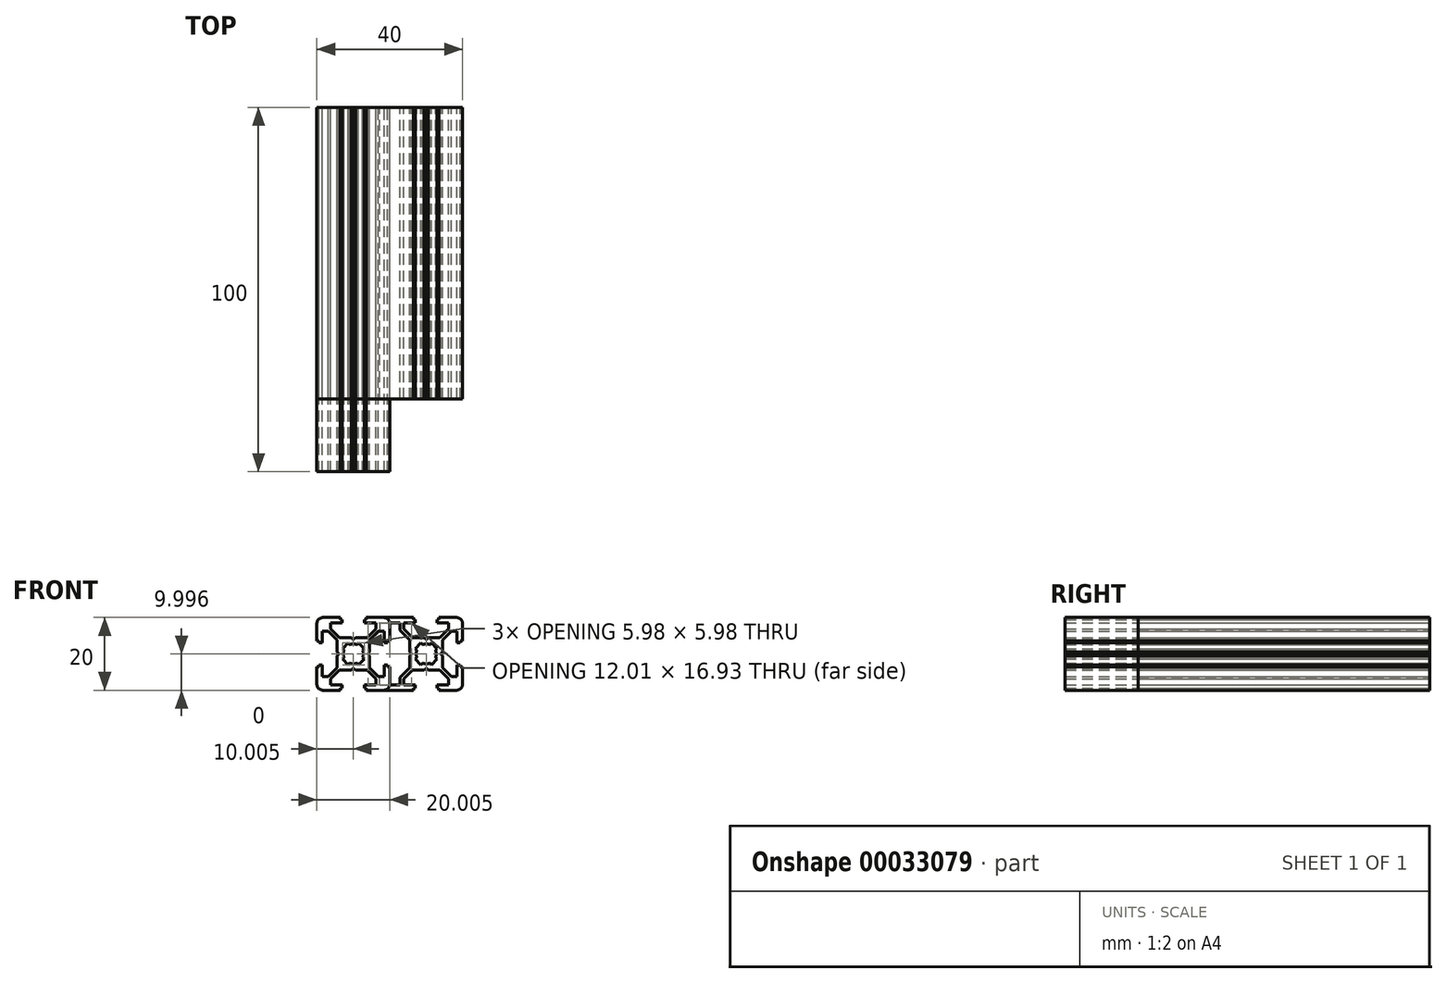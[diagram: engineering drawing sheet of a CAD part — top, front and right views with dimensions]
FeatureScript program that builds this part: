
annotation { "Feature Type Name" : "Feature", "Feature Type Description" : "" }
export const myFeature = defineFeature(function(context is Context, id is Id, definition is map)
    precondition{}
    {
        {
            var Q0;
            Q0=qCreatedBy(makeId("Front.planeOp"),FACE);
            var sketch = newSketch(context, id + "F0", { "sketchPlane" : qUnion([Q0])});
            skLineSegment(sketch, "E0.rect.bottom", {"start": v(-8.26, 10.09) * mm, "end": v(-3.52, 10.09) * mm});
            skLineSegment(sketch, "E0.rect.top", {"start": v(-8.26, -9.91) * mm, "end": v(-3.52, -9.91) * mm});
            skLineSegment(sketch, "E0.rect.left", {"start": v(-10, 8.34) * mm, "end": v(-10, 3.6) * mm});
            skLineSegment(sketch, "E0.rect.right", {"start": v(10, 8.34) * mm, "end": v(10, 3.6) * mm});
            skPoint(sketch, "E0.rect.middle", {"position": v(0, 0.09) * mm});
            skPoint(sketch, "E1.visualSharp", {"position": v(-10, 10.09) * mm});
            skArc(sketch, "E1.filletArc", {"start": v(-8.26, 10.09) * mm, "mid": v(-9.5, 9.57) * mm, "end": v(-10, 8.34) * mm});
            skPoint(sketch, "E2.visualSharp", {"position": v(10, 10.09) * mm});
            skArc(sketch, "E2.filletArc", {"start": v(10, 8.34) * mm, "mid": v(9.48, 9.57) * mm, "end": v(8.24, 10.09) * mm});
            skPoint(sketch, "E3.visualSharp", {"position": v(10, -9.91) * mm});
            skArc(sketch, "E3.filletArc", {"start": v(8.24, -9.91) * mm, "mid": v(9.48, -9.4) * mm, "end": v(10, -8.16) * mm});
            skPoint(sketch, "E4.visualSharp", {"position": v(-10, -9.91) * mm});
            skArc(sketch, "E4.filletArc", {"start": v(-10, -8.16) * mm, "mid": v(-9.5, -9.4) * mm, "end": v(-8.26, -9.91) * mm});
            skPoint(sketch, "E5.rect.middle", {"position": v(-10, 0.09) * mm});
            skPoint(sketch, "E6.rect.middle", {"position": v(0, -9.91) * mm});
            skPoint(sketch, "E7.4.MirrorP", {"position": v(0, 10.09) * mm});
            skPoint(sketch, "E8.4.MirrorP", {"position": v(10, 0.09) * mm});
            skLineSegment(sketch, "E9", {"start": v(-3, 9.47) * mm, "end": v(-3, 8.55) * mm});
            skLineSegment(sketch, "E10", {"start": v(-3, 8.55) * mm, "end": v(-6.2, 8.55) * mm});
            skLineSegment(sketch, "E11", {"start": v(-6.2, 8.55) * mm, "end": v(-6.2, 6.99) * mm});
            skLineSegment(sketch, "E12", {"start": v(-0.58, 4.59) * mm, "end": v(-3.8, 4.59) * mm});
            skLineSegment(sketch, "E13", {"start": v(-3.8, 4.59) * mm, "end": v(-6.2, 6.99) * mm});
            skLineSegment(sketch, "E14", {"start": v(-3.52, 10.09) * mm, "end": v(-3.52, 9.47) * mm});
            skLineSegment(sketch, "E15", {"start": v(-3.52, 9.47) * mm, "end": v(-3, 9.47) * mm});
            skLineSegment(sketch, "E16", {"start": v(0, 28.9) * mm, "end": v(0, 4.59) * mm});
            skLineSegment(sketch, "E17.0.MirrorCS", {"start": v(3.51, 10.09) * mm, "end": v(3.51, 9.47) * mm});
            skLineSegment(sketch, "E18.0.MirrorCS", {"start": v(3.51, 9.47) * mm, "end": v(3, 9.47) * mm});
            skLineSegment(sketch, "E19.0.MirrorCS", {"start": v(3, 8.55) * mm, "end": v(6.2, 8.55) * mm});
            skLineSegment(sketch, "E20.0.MirrorCS", {"start": v(6.2, 8.55) * mm, "end": v(6.2, 6.99) * mm});
            skLineSegment(sketch, "E21.0.MirrorCS", {"start": v(3.8, 4.59) * mm, "end": v(6.2, 6.99) * mm});
            skLineSegment(sketch, "E22.0.MirrorCS", {"start": v(3.51, -9.91) * mm, "end": v(3.51, -9.3) * mm});
            skLineSegment(sketch, "E23.0.MirrorCS", {"start": v(3.51, -9.3) * mm, "end": v(3, -9.3) * mm});
            skLineSegment(sketch, "E24.0.MirrorCS", {"start": v(3, -8.38) * mm, "end": v(6.2, -8.38) * mm});
            skLineSegment(sketch, "E25.0.MirrorCS", {"start": v(6.2, -8.38) * mm, "end": v(6.2, -6.81) * mm});
            skLineSegment(sketch, "E26.0.MirrorCS", {"start": v(3.8, -4.41) * mm, "end": v(6.2, -6.81) * mm});
            skLineSegment(sketch, "E27.0.MirrorCS", {"start": v(-0.58, -4.41) * mm, "end": v(-3.8, -4.41) * mm});
            skLineSegment(sketch, "E28.0.MirrorCS", {"start": v(-3.8, -4.41) * mm, "end": v(-6.2, -6.81) * mm});
            skLineSegment(sketch, "E29.0.MirrorCS", {"start": v(-6.2, -8.38) * mm, "end": v(-6.2, -6.81) * mm});
            skLineSegment(sketch, "E30.0.MirrorCS", {"start": v(-3, -8.38) * mm, "end": v(-6.2, -8.38) * mm});
            skLineSegment(sketch, "E31.0.MirrorCS", {"start": v(-3.52, -9.3) * mm, "end": v(-3, -9.3) * mm});
            skLineSegment(sketch, "E32.0.MirrorCS", {"start": v(-3.52, -9.91) * mm, "end": v(-3.52, -9.3) * mm});
            skLineSegment(sketch, "E33.0.MirrorCS", {"start": v(10, 3.6) * mm, "end": v(9.38, 3.6) * mm});
            skLineSegment(sketch, "E34.0.MirrorCS", {"start": v(9.38, 3.6) * mm, "end": v(9.38, 3.09) * mm});
            skLineSegment(sketch, "E35.0.MirrorCS", {"start": v(8.46, 3.09) * mm, "end": v(8.46, 6.29) * mm});
            skLineSegment(sketch, "E36.0.MirrorCS", {"start": v(8.46, 6.29) * mm, "end": v(6.9, 6.29) * mm});
            skLineSegment(sketch, "E37.0.MirrorCS", {"start": v(4.5, 3.89) * mm, "end": v(6.9, 6.29) * mm});
            skLineSegment(sketch, "E38.0.MirrorCS", {"start": v(4.5, 0.56) * mm, "end": v(4.5, 3.89) * mm});
            skLineSegment(sketch, "E39.0.MirrorCS", {"start": v(4.5, -3.71) * mm, "end": v(6.9, -6.11) * mm});
            skLineSegment(sketch, "E40.0.MirrorCS", {"start": v(8.46, -6.11) * mm, "end": v(6.9, -6.11) * mm});
            skLineSegment(sketch, "E41.0.MirrorCS", {"start": v(8.46, -2.91) * mm, "end": v(8.46, -6.11) * mm});
            skLineSegment(sketch, "E42.0.MirrorCS", {"start": v(9.38, -3.43) * mm, "end": v(9.38, -2.91) * mm});
            skLineSegment(sketch, "E43.0.MirrorCS", {"start": v(10, -3.43) * mm, "end": v(9.38, -3.43) * mm});
            skLineSegment(sketch, "E44.0.MirrorCS", {"start": v(-4.5, -3.71) * mm, "end": v(-6.9, -6.11) * mm});
            skLineSegment(sketch, "E45.0.MirrorCS", {"start": v(-8.47, -6.11) * mm, "end": v(-6.9, -6.11) * mm});
            skLineSegment(sketch, "E46.0.MirrorCS", {"start": v(-8.47, -2.91) * mm, "end": v(-8.47, -6.11) * mm});
            skLineSegment(sketch, "E47.0.MirrorCS", {"start": v(-4.5, 3.89) * mm, "end": v(-6.9, 6.29) * mm});
            skLineSegment(sketch, "E48.0.MirrorCS", {"start": v(-8.47, 6.29) * mm, "end": v(-6.9, 6.29) * mm});
            skLineSegment(sketch, "E49.0.MirrorCS", {"start": v(-8.47, 3.09) * mm, "end": v(-8.47, 6.29) * mm});
            skLineSegment(sketch, "E50.0.MirrorCS", {"start": v(-9.39, 3.6) * mm, "end": v(-9.39, 3.09) * mm});
            skLineSegment(sketch, "E51.0.MirrorCS", {"start": v(-10, 3.6) * mm, "end": v(-9.39, 3.6) * mm});
            skLineSegment(sketch, "E52.0.MirrorCS", {"start": v(-9.39, -3.43) * mm, "end": v(-9.39, -2.91) * mm});
            skLineSegment(sketch, "E53.0.MirrorCS", {"start": v(-10, -3.43) * mm, "end": v(-9.39, -3.43) * mm});
            skPoint(sketch, "E54", {"position": v(3, 10.09) * mm});
            skPoint(sketch, "E55", {"position": v(-3, 9.47) * mm});
            skPoint(sketch, "E56", {"position": v(-3, 10.09) * mm});
            skPoint(sketch, "E57", {"position": v(3, 9.47) * mm});
            skPoint(sketch, "E58", {"position": v(3.51, 10.09) * mm});
            skPoint(sketch, "E59", {"position": v(-3, 8.55) * mm});
            skPoint(sketch, "E60", {"position": v(-6.2, 8.55) * mm});
            skPoint(sketch, "E61", {"position": v(-6.2, 6.99) * mm});
            skPoint(sketch, "E62", {"position": v(-3.8, 4.59) * mm});
            skPoint(sketch, "E63", {"position": v(3.8, 4.59) * mm});
            skPoint(sketch, "E64", {"position": v(6.2, 6.99) * mm});
            skPoint(sketch, "E65", {"position": v(6.2, 8.55) * mm});
            skPoint(sketch, "E66", {"position": v(3, 8.55) * mm});
            skLineSegment(sketch, "E67.trimOffspring", {"start": v(3, 9.47) * mm, "end": v(3, 8.55) * mm});
            skLineSegment(sketch, "E68.trimOffspring", {"start": v(3.51, 10.09) * mm, "end": v(8.24, 10.09) * mm});
            skPoint(sketch, "E69.orphan", {"position": v(-3, 15.59) * mm});
            skPoint(sketch, "E7.2.MirrorCS.end.orphan", {"position": v(3, 15.59) * mm});
            skPoint(sketch, "E70", {"position": v(-10, 3.6) * mm});
            skPoint(sketch, "E71", {"position": v(-10, 3.09) * mm});
            skPoint(sketch, "E72", {"position": v(-9.39, 3.6) * mm});
            skPoint(sketch, "E73", {"position": v(-9.39, 3.09) * mm});
            skPoint(sketch, "E74", {"position": v(-8.47, 3.09) * mm});
            skPoint(sketch, "E75", {"position": v(-8.47, 6.29) * mm});
            skPoint(sketch, "E76", {"position": v(-6.9, 6.29) * mm});
            skPoint(sketch, "E77", {"position": v(-4.5, 3.89) * mm});
            skPoint(sketch, "E78", {"position": v(-4.5, -3.71) * mm});
            skPoint(sketch, "E79", {"position": v(-6.9, -6.11) * mm});
            skPoint(sketch, "E80", {"position": v(-8.44, -6.12) * mm});
            skPoint(sketch, "E81", {"position": v(-8.47, -2.91) * mm});
            skPoint(sketch, "E82", {"position": v(-9.39, -2.91) * mm});
            skPoint(sketch, "E83", {"position": v(-9.39, -3.43) * mm});
            skPoint(sketch, "E84", {"position": v(-10, -3.43) * mm});
            skPoint(sketch, "E85", {"position": v(-10, -2.91) * mm});
            skPoint(sketch, "E86", {"position": v(-3.52, -9.91) * mm});
            skPoint(sketch, "E87", {"position": v(-3, -9.91) * mm});
            skPoint(sketch, "E88", {"position": v(-3, -9.3) * mm});
            skPoint(sketch, "E89", {"position": v(-3.52, -9.3) * mm});
            skPoint(sketch, "E90", {"position": v(-3, -8.38) * mm});
            skPoint(sketch, "E91", {"position": v(-6.2, -8.38) * mm});
            skPoint(sketch, "E92", {"position": v(-6.2, -6.81) * mm});
            skPoint(sketch, "E93", {"position": v(-3.8, -4.41) * mm});
            skPoint(sketch, "E94", {"position": v(3.8, -4.41) * mm});
            skPoint(sketch, "E95", {"position": v(6.2, -6.81) * mm});
            skPoint(sketch, "E96", {"position": v(6.2, -8.38) * mm});
            skPoint(sketch, "E97", {"position": v(3, -8.38) * mm});
            skPoint(sketch, "E98", {"position": v(3, -9.3) * mm});
            skPoint(sketch, "E99", {"position": v(3.51, -9.3) * mm});
            skPoint(sketch, "E100", {"position": v(3, -9.91) * mm});
            skPoint(sketch, "E101", {"position": v(3.51, -9.91) * mm});
            skPoint(sketch, "E102", {"position": v(10, -3.43) * mm});
            skPoint(sketch, "E103", {"position": v(10, -2.91) * mm});
            skPoint(sketch, "E104", {"position": v(9.38, -2.91) * mm});
            skPoint(sketch, "E105", {"position": v(9.38, -3.43) * mm});
            skPoint(sketch, "E106", {"position": v(8.46, -2.91) * mm});
            skPoint(sketch, "E107", {"position": v(8.46, -6.11) * mm});
            skPoint(sketch, "E108", {"position": v(6.9, -6.11) * mm});
            skPoint(sketch, "E109", {"position": v(4.5, -3.71) * mm});
            skPoint(sketch, "E110", {"position": v(4.5, 3.89) * mm});
            skPoint(sketch, "E111", {"position": v(6.9, 6.29) * mm});
            skPoint(sketch, "E112", {"position": v(8.46, 6.29) * mm});
            skPoint(sketch, "E113", {"position": v(8.46, 3.09) * mm});
            skPoint(sketch, "E114", {"position": v(9.38, 3.09) * mm});
            skPoint(sketch, "E115", {"position": v(9.38, 3.6) * mm});
            skPoint(sketch, "E116", {"position": v(10, 3.6) * mm});
            skPoint(sketch, "E117", {"position": v(10, 3.09) * mm});
            skLineSegment(sketch, "E118.trimOffspring", {"start": v(10, -3.43) * mm, "end": v(10, -8.16) * mm});
            skLineSegment(sketch, "E119.trimOffspring", {"start": v(9.38, 3.09) * mm, "end": v(8.46, 3.09) * mm});
            skPoint(sketch, "E8.1.MirrorCS.start.orphan", {"position": v(15.5, 3.09) * mm});
            skLineSegment(sketch, "E120.trimOffspring", {"start": v(9.38, -2.91) * mm, "end": v(8.46, -2.91) * mm});
            skPoint(sketch, "E8.2.MirrorCS.start.orphan", {"position": v(15.5, -2.91) * mm});
            skLineSegment(sketch, "E121.trimOffspring", {"start": v(3.51, -9.91) * mm, "end": v(8.24, -9.91) * mm});
            skLineSegment(sketch, "E122.trimOffspring", {"start": v(3, -9.3) * mm, "end": v(3, -8.38) * mm});
            skLineSegment(sketch, "E123.trimOffspring", {"start": v(-3, -9.3) * mm, "end": v(-3, -8.38) * mm});
            skPoint(sketch, "E124.orphan", {"position": v(3, -15.41) * mm});
            skPoint(sketch, "E6.rect.bottom.start.orphan", {"position": v(-3, -15.41) * mm});
            skLineSegment(sketch, "E125.trimOffspring", {"start": v(-10, -3.43) * mm, "end": v(-10, -8.16) * mm});
            skLineSegment(sketch, "E126.trimOffspring", {"start": v(-9.39, -2.91) * mm, "end": v(-8.47, -2.91) * mm});
            skLineSegment(sketch, "E127.trimOffspring", {"start": v(-9.39, 3.09) * mm, "end": v(-8.47, 3.09) * mm});
            skPoint(sketch, "E5.rect.left.end.orphan", {"position": v(-15.5, -2.91) * mm});
            skPoint(sketch, "E5.rect.left.start.orphan", {"position": v(-15.5, 3.09) * mm});
            skArc(sketch, "E128", {"start": v(1.01, 2.64) * mm, "mid": v(0, 2.84) * mm, "end": v(-1.02, 2.64) * mm});
            skLineSegment(sketch, "E129", {"start": v(-0.58, 4.59) * mm, "end": v(0, 4.02) * mm});
            skLineSegment(sketch, "E130", {"start": v(-4.5, 0.56) * mm, "end": v(-4, 0.09) * mm});
            skLineSegment(sketch, "E131.0.MirrorCS", {"start": v(0.57, 4.59) * mm, "end": v(0, 4.02) * mm});
            skLineSegment(sketch, "E132.0.MirrorCS", {"start": v(4.5, 0.56) * mm, "end": v(4, 0.09) * mm});
            skLineSegment(sketch, "E133.0.MirrorCS", {"start": v(-4.5, -0.4) * mm, "end": v(-4, 0.09) * mm});
            skLineSegment(sketch, "E134.0.MirrorCS", {"start": v(4.5, -0.4) * mm, "end": v(4, 0.09) * mm});
            skLineSegment(sketch, "E135.0.MirrorCS", {"start": v(0.57, -4.41) * mm, "end": v(0, -3.84) * mm});
            skLineSegment(sketch, "E136.0.MirrorCS", {"start": v(-0.58, -4.41) * mm, "end": v(0, -3.84) * mm});
            skPoint(sketch, "E137.orphan", {"position": v(0, -4.41) * mm});
            skLineSegment(sketch, "E138", {"start": v(8.24, -8.16) * mm, "end": v(-10.9, 10.99) * mm, "construction": true});
            skLineSegment(sketch, "E139", {"start": v(-5.8, -1.82) * mm, "end": v(1.97, 5.95) * mm, "construction": true});
            skLineSegment(sketch, "E140", {"start": v(-3, 1.54) * mm, "end": v(-2.56, 1.1) * mm});
            skLineSegment(sketch, "E141.0.MirrorCS", {"start": v(-1.46, 3.08) * mm, "end": v(-1.02, 2.64) * mm});
            skLineSegment(sketch, "E142.0.MirrorCS", {"start": v(1.45, 3.08) * mm, "end": v(1.01, 2.64) * mm});
            skLineSegment(sketch, "E143.0.MirrorCS", {"start": v(2.98, 1.54) * mm, "end": v(2.55, 1.1) * mm});
            skLineSegment(sketch, "E144.0.MirrorCS", {"start": v(2.98, -1.37) * mm, "end": v(2.55, -0.93) * mm});
            skLineSegment(sketch, "E145.0.MirrorCS", {"start": v(1.45, -2.9) * mm, "end": v(1.01, -2.47) * mm});
            skLineSegment(sketch, "E146.0.MirrorCS", {"start": v(-1.46, -2.9) * mm, "end": v(-1.02, -2.47) * mm});
            skLineSegment(sketch, "E147.0.MirrorCS", {"start": v(-3, -1.37) * mm, "end": v(-2.56, -0.93) * mm});
            skArc(sketch, "E148.trimOffspring", {"start": v(-1.02, -2.47) * mm, "mid": v(0, -2.66) * mm, "end": v(1.01, -2.47) * mm});
            skArc(sketch, "E149.trimOffspring", {"start": v(2.55, -0.93) * mm, "mid": v(2.74, 0.09) * mm, "end": v(2.55, 1.1) * mm});
            skArc(sketch, "E150.trimOffspring", {"start": v(-2.56, 1.1) * mm, "mid": v(-2.76, 0.09) * mm, "end": v(-2.56, -0.93) * mm});
            skLineSegment(sketch, "E151", {"start": v(-3, -1.37) * mm, "end": v(-1.46, -2.9) * mm});
            skLineSegment(sketch, "E152", {"start": v(1.45, 3.08) * mm, "end": v(2.98, 1.54) * mm});
            skLineSegment(sketch, "E153", {"start": v(-1.46, 3.08) * mm, "end": v(-3, 1.54) * mm});
            skLineSegment(sketch, "E154", {"start": v(2.98, -1.37) * mm, "end": v(1.45, -2.9) * mm});
            skLineSegment(sketch, "E155", {"start": v(-4.5, 3.89) * mm, "end": v(-4.5, 0.56) * mm});
            skLineSegment(sketch, "E156", {"start": v(-4.5, -0.4) * mm, "end": v(-4.5, -3.71) * mm});
            skLineSegment(sketch, "E157", {"start": v(4.5, -0.4) * mm, "end": v(4.5, -3.71) * mm});
            skLineSegment(sketch, "E158", {"start": v(0.57, 4.59) * mm, "end": v(3.8, 4.59) * mm});
            skLineSegment(sketch, "E159", {"start": v(0.57, -4.41) * mm, "end": v(3.8, -4.41) * mm});
            skSolve(sketch);
        }
        {
            var Q0;
            Q0=qCreatedBy(makeId("Front.planeOp"),FACE);
            var sketch = newSketch(context, id + "F1", { "sketchPlane" : qUnion([Q0])});
            skLineSegment(sketch, "E160.0.0", {"start": v(-3.52, 10.09) * mm, "end": v(-8.26, 10.09) * mm});
            skArc(sketch, "E160.0.1", {"start": v(-8.26, 10.09) * mm, "mid": v(-9.5, 9.57) * mm, "end": v(-10, 8.34) * mm});
            skLineSegment(sketch, "E160.0.2", {"start": v(-10, 8.34) * mm, "end": v(-10, 3.6) * mm});
            skLineSegment(sketch, "E160.0.3", {"start": v(-10, 3.6) * mm, "end": v(-9.39, 3.6) * mm});
            skLineSegment(sketch, "E160.0.4", {"start": v(-9.39, 3.6) * mm, "end": v(-9.39, 3.09) * mm});
            skLineSegment(sketch, "E160.0.5", {"start": v(-9.39, 3.09) * mm, "end": v(-8.47, 3.09) * mm});
            skLineSegment(sketch, "E160.0.6", {"start": v(-8.47, 3.09) * mm, "end": v(-8.47, 6.29) * mm});
            skLineSegment(sketch, "E160.0.7", {"start": v(-8.47, 6.29) * mm, "end": v(-6.9, 6.29) * mm});
            skLineSegment(sketch, "E160.0.8", {"start": v(-6.9, 6.29) * mm, "end": v(-4.5, 3.89) * mm});
            skLineSegment(sketch, "E160.0.9", {"start": v(-4.5, 3.89) * mm, "end": v(-4.5, 0.56) * mm});
            skLineSegment(sketch, "E160.0.10", {"start": v(-4.5, 0.56) * mm, "end": v(-4, 0.09) * mm});
            skLineSegment(sketch, "E160.0.11", {"start": v(-4, 0.09) * mm, "end": v(-4.5, -0.4) * mm});
            skLineSegment(sketch, "E160.0.12", {"start": v(-4.5, -0.4) * mm, "end": v(-4.5, -3.71) * mm});
            skLineSegment(sketch, "E160.0.13", {"start": v(-4.5, -3.71) * mm, "end": v(-6.9, -6.11) * mm});
            skLineSegment(sketch, "E160.0.14", {"start": v(-6.9, -6.11) * mm, "end": v(-8.47, -6.11) * mm});
            skLineSegment(sketch, "E160.0.15", {"start": v(-8.47, -6.11) * mm, "end": v(-8.47, -2.91) * mm});
            skLineSegment(sketch, "E160.0.16", {"start": v(-8.47, -2.91) * mm, "end": v(-9.39, -2.91) * mm});
            skLineSegment(sketch, "E160.0.17", {"start": v(-9.39, -2.91) * mm, "end": v(-9.39, -3.43) * mm});
            skLineSegment(sketch, "E160.0.18", {"start": v(-9.39, -3.43) * mm, "end": v(-10, -3.43) * mm});
            skLineSegment(sketch, "E160.0.19", {"start": v(-10, -3.43) * mm, "end": v(-10, -8.16) * mm});
            skArc(sketch, "E160.0.20", {"start": v(-10, -8.16) * mm, "mid": v(-9.5, -9.4) * mm, "end": v(-8.26, -9.91) * mm});
            skLineSegment(sketch, "E160.0.21", {"start": v(-8.26, -9.91) * mm, "end": v(-3.52, -9.91) * mm});
            skLineSegment(sketch, "E160.0.22", {"start": v(-3.52, -9.91) * mm, "end": v(-3.52, -9.3) * mm});
            skLineSegment(sketch, "E160.0.23", {"start": v(-3.52, -9.3) * mm, "end": v(-3, -9.3) * mm});
            skLineSegment(sketch, "E160.0.24", {"start": v(-3, -9.3) * mm, "end": v(-3, -8.38) * mm});
            skLineSegment(sketch, "E160.0.25", {"start": v(-3, -8.38) * mm, "end": v(-6.2, -8.38) * mm});
            skLineSegment(sketch, "E160.0.26", {"start": v(-6.2, -8.38) * mm, "end": v(-6.2, -6.81) * mm});
            skLineSegment(sketch, "E160.0.27", {"start": v(-6.2, -6.81) * mm, "end": v(-3.8, -4.41) * mm});
            skLineSegment(sketch, "E160.0.28", {"start": v(-3.8, -4.41) * mm, "end": v(-0.58, -4.41) * mm});
            skLineSegment(sketch, "E160.0.29", {"start": v(-0.58, -4.41) * mm, "end": v(0, -3.84) * mm});
            skLineSegment(sketch, "E160.0.30", {"start": v(0, -3.84) * mm, "end": v(0.57, -4.41) * mm});
            skLineSegment(sketch, "E160.0.31", {"start": v(0.57, -4.41) * mm, "end": v(3.8, -4.41) * mm});
            skLineSegment(sketch, "E160.0.32", {"start": v(3.8, -4.41) * mm, "end": v(6.2, -6.81) * mm});
            skLineSegment(sketch, "E160.0.33", {"start": v(6.2, -6.81) * mm, "end": v(6.2, -8.38) * mm});
            skLineSegment(sketch, "E160.0.34", {"start": v(6.2, -8.38) * mm, "end": v(3, -8.38) * mm});
            skLineSegment(sketch, "E160.0.35", {"start": v(3, -8.38) * mm, "end": v(3, -9.3) * mm});
            skLineSegment(sketch, "E160.0.36", {"start": v(3, -9.3) * mm, "end": v(3.51, -9.3) * mm});
            skLineSegment(sketch, "E160.0.37", {"start": v(3.51, -9.3) * mm, "end": v(3.51, -9.91) * mm});
            skLineSegment(sketch, "E160.0.47", {"start": v(4.5, -3.71) * mm, "end": v(4.5, -0.4) * mm});
            skLineSegment(sketch, "E160.0.48", {"start": v(4.5, -0.4) * mm, "end": v(4, 0.09) * mm});
            skLineSegment(sketch, "E160.0.49", {"start": v(4, 0.09) * mm, "end": v(4.5, 0.56) * mm});
            skLineSegment(sketch, "E160.0.50", {"start": v(4.5, 0.56) * mm, "end": v(4.5, 3.89) * mm});
            skLineSegment(sketch, "E160.0.60", {"start": v(3.51, 10.09) * mm, "end": v(3.51, 9.47) * mm});
            skLineSegment(sketch, "E160.0.61", {"start": v(3.51, 9.47) * mm, "end": v(3, 9.47) * mm});
            skLineSegment(sketch, "E160.0.62", {"start": v(3, 9.47) * mm, "end": v(3, 8.55) * mm});
            skLineSegment(sketch, "E160.0.63", {"start": v(3, 8.55) * mm, "end": v(6.2, 8.55) * mm});
            skLineSegment(sketch, "E160.0.64", {"start": v(6.2, 8.55) * mm, "end": v(6.2, 6.99) * mm});
            skLineSegment(sketch, "E160.0.65", {"start": v(6.2, 6.99) * mm, "end": v(3.8, 4.59) * mm});
            skLineSegment(sketch, "E160.0.66", {"start": v(3.8, 4.59) * mm, "end": v(0.57, 4.59) * mm});
            skLineSegment(sketch, "E160.0.67", {"start": v(0.57, 4.59) * mm, "end": v(0, 4.02) * mm});
            skLineSegment(sketch, "E160.0.68", {"start": v(0, 4.02) * mm, "end": v(-0.58, 4.59) * mm});
            skLineSegment(sketch, "E160.0.69", {"start": v(-0.58, 4.59) * mm, "end": v(-3.8, 4.59) * mm});
            skLineSegment(sketch, "E160.0.70", {"start": v(-3.8, 4.59) * mm, "end": v(-6.2, 6.99) * mm});
            skLineSegment(sketch, "E160.0.71", {"start": v(-6.2, 6.99) * mm, "end": v(-6.2, 8.55) * mm});
            skLineSegment(sketch, "E160.0.72", {"start": v(-6.2, 8.55) * mm, "end": v(-3, 8.55) * mm});
            skLineSegment(sketch, "E160.0.73", {"start": v(-3, 8.55) * mm, "end": v(-3, 9.47) * mm});
            skLineSegment(sketch, "E160.0.74", {"start": v(-3, 9.47) * mm, "end": v(-3.52, 9.47) * mm});
            skLineSegment(sketch, "E160.0.75", {"start": v(-3.52, 9.47) * mm, "end": v(-3.52, 10.09) * mm});
            skLineSegment(sketch, "E161.0.0", {"start": v(1.45, 3.08) * mm, "end": v(1.01, 2.64) * mm});
            skArc(sketch, "E161.0.1", {"start": v(1.01, 2.64) * mm, "mid": v(0, 2.84) * mm, "end": v(-1.02, 2.64) * mm});
            skLineSegment(sketch, "E161.0.2", {"start": v(-1.02, 2.64) * mm, "end": v(-1.46, 3.08) * mm});
            skLineSegment(sketch, "E161.0.3", {"start": v(-1.46, 3.08) * mm, "end": v(-3, 1.54) * mm});
            skLineSegment(sketch, "E161.0.4", {"start": v(-3, 1.54) * mm, "end": v(-2.56, 1.1) * mm});
            skArc(sketch, "E161.0.5", {"start": v(-2.56, 1.1) * mm, "mid": v(-2.76, 0.09) * mm, "end": v(-2.56, -0.93) * mm});
            skLineSegment(sketch, "E161.0.6", {"start": v(-2.56, -0.93) * mm, "end": v(-3, -1.37) * mm});
            skLineSegment(sketch, "E161.0.7", {"start": v(-3, -1.37) * mm, "end": v(-1.46, -2.9) * mm});
            skLineSegment(sketch, "E161.0.8", {"start": v(-1.46, -2.9) * mm, "end": v(-1.02, -2.47) * mm});
            skArc(sketch, "E161.0.9", {"start": v(-1.02, -2.47) * mm, "mid": v(0, -2.66) * mm, "end": v(1.01, -2.47) * mm});
            skLineSegment(sketch, "E161.0.10", {"start": v(1.01, -2.47) * mm, "end": v(1.45, -2.9) * mm});
            skLineSegment(sketch, "E161.0.11", {"start": v(1.45, -2.9) * mm, "end": v(2.98, -1.37) * mm});
            skLineSegment(sketch, "E161.0.12", {"start": v(2.98, -1.37) * mm, "end": v(2.55, -0.93) * mm});
            skArc(sketch, "E161.0.13", {"start": v(2.55, -0.93) * mm, "mid": v(2.74, 0.09) * mm, "end": v(2.55, 1.1) * mm});
            skLineSegment(sketch, "E161.0.14", {"start": v(2.55, 1.1) * mm, "end": v(2.98, 1.54) * mm});
            skLineSegment(sketch, "E161.0.15", {"start": v(2.98, 1.54) * mm, "end": v(1.45, 3.08) * mm});
            skLineSegment(sketch, "E162", {"start": v(10, 11.4) * mm, "end": v(10, -11.43) * mm, "construction": true});
            skLineSegment(sketch, "E163.0.MirrorCS", {"start": v(16.48, 10.09) * mm, "end": v(16.48, 9.47) * mm});
            skLineSegment(sketch, "E164.0.MirrorCS", {"start": v(16.48, 9.47) * mm, "end": v(17, 9.47) * mm});
            skLineSegment(sketch, "E165.0.MirrorCS", {"start": v(17, 9.47) * mm, "end": v(17, 8.55) * mm});
            skLineSegment(sketch, "E166.0.MirrorCS", {"start": v(17, 8.55) * mm, "end": v(13.8, 8.55) * mm});
            skLineSegment(sketch, "E167.0.MirrorCS", {"start": v(13.8, 8.55) * mm, "end": v(13.8, 6.99) * mm});
            skLineSegment(sketch, "E168.0.MirrorCS", {"start": v(13.8, 6.99) * mm, "end": v(16.2, 4.59) * mm});
            skLineSegment(sketch, "E169.0.MirrorCS", {"start": v(16.2, 4.59) * mm, "end": v(19.42, 4.59) * mm});
            skLineSegment(sketch, "E170.0.MirrorCS", {"start": v(19.42, 4.59) * mm, "end": v(20, 4.02) * mm});
            skLineSegment(sketch, "E171.0.MirrorCS", {"start": v(20, 4.02) * mm, "end": v(20.57, 4.59) * mm});
            skLineSegment(sketch, "E172.0.MirrorCS", {"start": v(20.57, 4.59) * mm, "end": v(23.8, 4.59) * mm});
            skLineSegment(sketch, "E173.0.MirrorCS", {"start": v(23.8, 4.59) * mm, "end": v(26.2, 6.99) * mm});
            skLineSegment(sketch, "E174.0.MirrorCS", {"start": v(26.2, 6.99) * mm, "end": v(26.2, 8.55) * mm});
            skLineSegment(sketch, "E175.0.MirrorCS", {"start": v(26.2, 8.55) * mm, "end": v(23, 8.55) * mm});
            skLineSegment(sketch, "E176.0.MirrorCS", {"start": v(23, 8.55) * mm, "end": v(23, 9.47) * mm});
            skLineSegment(sketch, "E177.0.MirrorCS", {"start": v(23, 9.47) * mm, "end": v(23.51, 9.47) * mm});
            skLineSegment(sketch, "E178.0.MirrorCS", {"start": v(23.51, 9.47) * mm, "end": v(23.51, 10.09) * mm});
            skLineSegment(sketch, "E179.0.MirrorCS", {"start": v(23.51, 10.09) * mm, "end": v(28.24, 10.09) * mm});
            skArc(sketch, "E180.0.MirrorCS", {"start": v(28.24, 10.09) * mm, "mid": v(29.48, 9.57) * mm, "end": v(30, 8.34) * mm});
            skLineSegment(sketch, "E181.0.MirrorCS", {"start": v(30, 8.34) * mm, "end": v(30, 3.6) * mm});
            skLineSegment(sketch, "E182.0.MirrorCS", {"start": v(30, 3.6) * mm, "end": v(29.38, 3.6) * mm});
            skLineSegment(sketch, "E183.0.MirrorCS", {"start": v(29.38, 3.6) * mm, "end": v(29.38, 3.09) * mm});
            skLineSegment(sketch, "E184.0.MirrorCS", {"start": v(29.38, 3.09) * mm, "end": v(28.46, 3.09) * mm});
            skLineSegment(sketch, "E185.0.MirrorCS", {"start": v(28.46, 3.09) * mm, "end": v(28.46, 6.29) * mm});
            skLineSegment(sketch, "E186.0.MirrorCS", {"start": v(28.46, 6.29) * mm, "end": v(26.9, 6.29) * mm});
            skLineSegment(sketch, "E187.0.MirrorCS", {"start": v(26.9, 6.29) * mm, "end": v(24.5, 3.89) * mm});
            skLineSegment(sketch, "E188.0.MirrorCS", {"start": v(24.5, 3.89) * mm, "end": v(24.5, 0.56) * mm});
            skLineSegment(sketch, "E189.0.MirrorCS", {"start": v(24.5, 0.56) * mm, "end": v(24, 0.09) * mm});
            skLineSegment(sketch, "E190.0.MirrorCS", {"start": v(24, 0.09) * mm, "end": v(24.5, -0.4) * mm});
            skLineSegment(sketch, "E191.0.MirrorCS", {"start": v(24.5, -0.4) * mm, "end": v(24.5, -3.71) * mm});
            skLineSegment(sketch, "E192.0.MirrorCS", {"start": v(24.5, -3.71) * mm, "end": v(26.9, -6.11) * mm});
            skLineSegment(sketch, "E193.0.MirrorCS", {"start": v(26.9, -6.11) * mm, "end": v(28.46, -6.11) * mm});
            skLineSegment(sketch, "E194.0.MirrorCS", {"start": v(28.46, -6.11) * mm, "end": v(28.46, -2.91) * mm});
            skLineSegment(sketch, "E195.0.MirrorCS", {"start": v(28.46, -2.91) * mm, "end": v(29.38, -2.91) * mm});
            skLineSegment(sketch, "E196.0.MirrorCS", {"start": v(29.38, -2.91) * mm, "end": v(29.38, -3.43) * mm});
            skLineSegment(sketch, "E197.0.MirrorCS", {"start": v(29.38, -3.43) * mm, "end": v(30, -3.43) * mm});
            skLineSegment(sketch, "E198.0.MirrorCS", {"start": v(30, -3.43) * mm, "end": v(30, -8.16) * mm});
            skArc(sketch, "E199.0.MirrorCS", {"start": v(30, -8.16) * mm, "mid": v(29.48, -9.4) * mm, "end": v(28.24, -9.91) * mm});
            skLineSegment(sketch, "E200.0.MirrorCS", {"start": v(28.24, -9.91) * mm, "end": v(23.51, -9.91) * mm});
            skLineSegment(sketch, "E201.0.MirrorCS", {"start": v(23.51, -9.91) * mm, "end": v(23.51, -9.3) * mm});
            skLineSegment(sketch, "E202.0.MirrorCS", {"start": v(23.51, -9.3) * mm, "end": v(23, -9.3) * mm});
            skLineSegment(sketch, "E203.0.MirrorCS", {"start": v(23, -9.3) * mm, "end": v(23, -8.38) * mm});
            skLineSegment(sketch, "E204.0.MirrorCS", {"start": v(23, -8.38) * mm, "end": v(26.2, -8.38) * mm});
            skLineSegment(sketch, "E205.0.MirrorCS", {"start": v(26.2, -8.38) * mm, "end": v(26.2, -6.81) * mm});
            skLineSegment(sketch, "E206.0.MirrorCS", {"start": v(26.2, -6.81) * mm, "end": v(23.8, -4.41) * mm});
            skLineSegment(sketch, "E207.0.MirrorCS", {"start": v(23.8, -4.41) * mm, "end": v(20.57, -4.41) * mm});
            skLineSegment(sketch, "E208.0.MirrorCS", {"start": v(20.57, -4.41) * mm, "end": v(20, -3.84) * mm});
            skLineSegment(sketch, "E209.0.MirrorCS", {"start": v(20, -3.84) * mm, "end": v(19.42, -4.41) * mm});
            skLineSegment(sketch, "E210.0.MirrorCS", {"start": v(19.42, -4.41) * mm, "end": v(16.2, -4.41) * mm});
            skLineSegment(sketch, "E211.0.MirrorCS", {"start": v(16.2, -4.41) * mm, "end": v(13.8, -6.81) * mm});
            skLineSegment(sketch, "E212.0.MirrorCS", {"start": v(13.8, -6.81) * mm, "end": v(13.8, -8.38) * mm});
            skLineSegment(sketch, "E213.0.MirrorCS", {"start": v(13.8, -8.38) * mm, "end": v(17, -8.38) * mm});
            skLineSegment(sketch, "E214.0.MirrorCS", {"start": v(17, -8.38) * mm, "end": v(17, -9.3) * mm});
            skLineSegment(sketch, "E215.0.MirrorCS", {"start": v(17, -9.3) * mm, "end": v(16.48, -9.3) * mm});
            skLineSegment(sketch, "E216.0.MirrorCS", {"start": v(16.48, -9.3) * mm, "end": v(16.48, -9.91) * mm});
            skLineSegment(sketch, "E217.0.MirrorCS", {"start": v(15.5, -3.71) * mm, "end": v(15.5, -0.4) * mm});
            skLineSegment(sketch, "E218.0.MirrorCS", {"start": v(15.5, -0.4) * mm, "end": v(16, 0.09) * mm});
            skLineSegment(sketch, "E219.0.MirrorCS", {"start": v(16, 0.09) * mm, "end": v(15.5, 0.56) * mm});
            skLineSegment(sketch, "E220.0.MirrorCS", {"start": v(15.5, 0.56) * mm, "end": v(15.5, 3.89) * mm});
            skArc(sketch, "E221.0.MirrorCS", {"start": v(17.44, -0.93) * mm, "mid": v(17.24, 0.09) * mm, "end": v(17.44, 1.1) * mm});
            skLineSegment(sketch, "E222.0.MirrorCS", {"start": v(17.44, 1.1) * mm, "end": v(17, 1.54) * mm});
            skLineSegment(sketch, "E223.0.MirrorCS", {"start": v(17, 1.54) * mm, "end": v(18.54, 3.08) * mm});
            skArc(sketch, "E224.0.MirrorCS", {"start": v(18.98, 2.64) * mm, "mid": v(20, 2.84) * mm, "end": v(21.01, 2.64) * mm});
            skLineSegment(sketch, "E225.0.MirrorCS", {"start": v(21.01, 2.64) * mm, "end": v(21.45, 3.08) * mm});
            skLineSegment(sketch, "E226.0.MirrorCS", {"start": v(21.45, 3.08) * mm, "end": v(22.98, 1.54) * mm});
            skLineSegment(sketch, "E227.0.MirrorCS", {"start": v(22.98, 1.54) * mm, "end": v(22.55, 1.1) * mm});
            skArc(sketch, "E228.0.MirrorCS", {"start": v(22.55, 1.1) * mm, "mid": v(22.74, 0.09) * mm, "end": v(22.55, -0.93) * mm});
            skLineSegment(sketch, "E229.0.MirrorCS", {"start": v(22.55, -0.93) * mm, "end": v(22.98, -1.37) * mm});
            skLineSegment(sketch, "E230.0.MirrorCS", {"start": v(22.98, -1.37) * mm, "end": v(21.45, -2.9) * mm});
            skLineSegment(sketch, "E231.0.MirrorCS", {"start": v(21.45, -2.9) * mm, "end": v(21.01, -2.47) * mm});
            skArc(sketch, "E232.0.MirrorCS", {"start": v(21.01, -2.47) * mm, "mid": v(20, -2.66) * mm, "end": v(18.98, -2.47) * mm});
            skLineSegment(sketch, "E233.0.MirrorCS", {"start": v(18.98, -2.47) * mm, "end": v(18.54, -2.9) * mm});
            skLineSegment(sketch, "E234.0.MirrorCS", {"start": v(18.54, -2.9) * mm, "end": v(17, -1.37) * mm});
            skLineSegment(sketch, "E235.0.MirrorCS", {"start": v(17, -1.37) * mm, "end": v(17.44, -0.93) * mm});
            skLineSegment(sketch, "E236.0.MirrorCS", {"start": v(18.54, 3.08) * mm, "end": v(18.98, 2.64) * mm});
            skLineSegment(sketch, "E237", {"start": v(3.51, 10.09) * mm, "end": v(16.48, 10.09) * mm});
            skLineSegment(sketch, "E238", {"start": v(3.51, -9.91) * mm, "end": v(16.48, -9.91) * mm});
            skLineSegment(sketch, "E239", {"start": v(0.8, 8.55) * mm, "end": v(20.5, 8.55) * mm, "construction": true});
            skLineSegment(sketch, "E240", {"start": v(0.52, -8.38) * mm, "end": v(20.42, -8.38) * mm, "construction": true});
            skLineSegment(sketch, "E241", {"start": v(4.5, -3.71) * mm, "end": v(12.34, -11.56) * mm, "construction": true});
            skLineSegment(sketch, "E242", {"start": v(15.5, -3.71) * mm, "end": v(7.46, -11.75) * mm, "construction": true});
            skLineSegment(sketch, "E243", {"start": v(4.5, 3.89) * mm, "end": v(12.58, 11.95) * mm, "construction": true});
            skLineSegment(sketch, "E244", {"start": v(15.5, 3.89) * mm, "end": v(7.44, 11.96) * mm, "construction": true});
            skLineSegment(sketch, "E245", {"start": v(7.18, 8.55) * mm, "end": v(7.18, 6.57) * mm});
            skLineSegment(sketch, "E246.0.MirrorCS", {"start": v(12.8, 8.55) * mm, "end": v(12.8, 6.57) * mm});
            skLineSegment(sketch, "E247", {"start": v(4.5, 3.89) * mm, "end": v(7.18, 6.57) * mm});
            skLineSegment(sketch, "E248", {"start": v(7.18, 8.55) * mm, "end": v(12.8, 8.55) * mm});
            skLineSegment(sketch, "E249", {"start": v(12.8, 6.57) * mm, "end": v(15.5, 3.89) * mm});
            skLineSegment(sketch, "E250", {"start": v(7.18, -8.38) * mm, "end": v(7.18, -6.4) * mm});
            skLineSegment(sketch, "E251", {"start": v(7.18, -6.4) * mm, "end": v(4.5, -3.71) * mm});
            skLineSegment(sketch, "E252", {"start": v(12.8, -8.38) * mm, "end": v(12.8, -6.4) * mm});
            skLineSegment(sketch, "E253", {"start": v(12.8, -6.4) * mm, "end": v(15.5, -3.71) * mm});
            skLineSegment(sketch, "E254", {"start": v(7.18, -8.38) * mm, "end": v(12.8, -8.38) * mm});
            skSolve(sketch);
        }
        {
            var Q0;
            Q0=qSketchRegion(id+"F0",true);
            extrude(context, id + "F2", {"entities" : qUnion([Q0]), "depth" : 100 * mm});
        }
        {
            var Q0;
            Q0=qSketchRegion(id+"F1",true);
            extrude(context, id + "F3", {"entities" : qUnion([Q0]), "depth" : 80 * mm});
        }
    });
